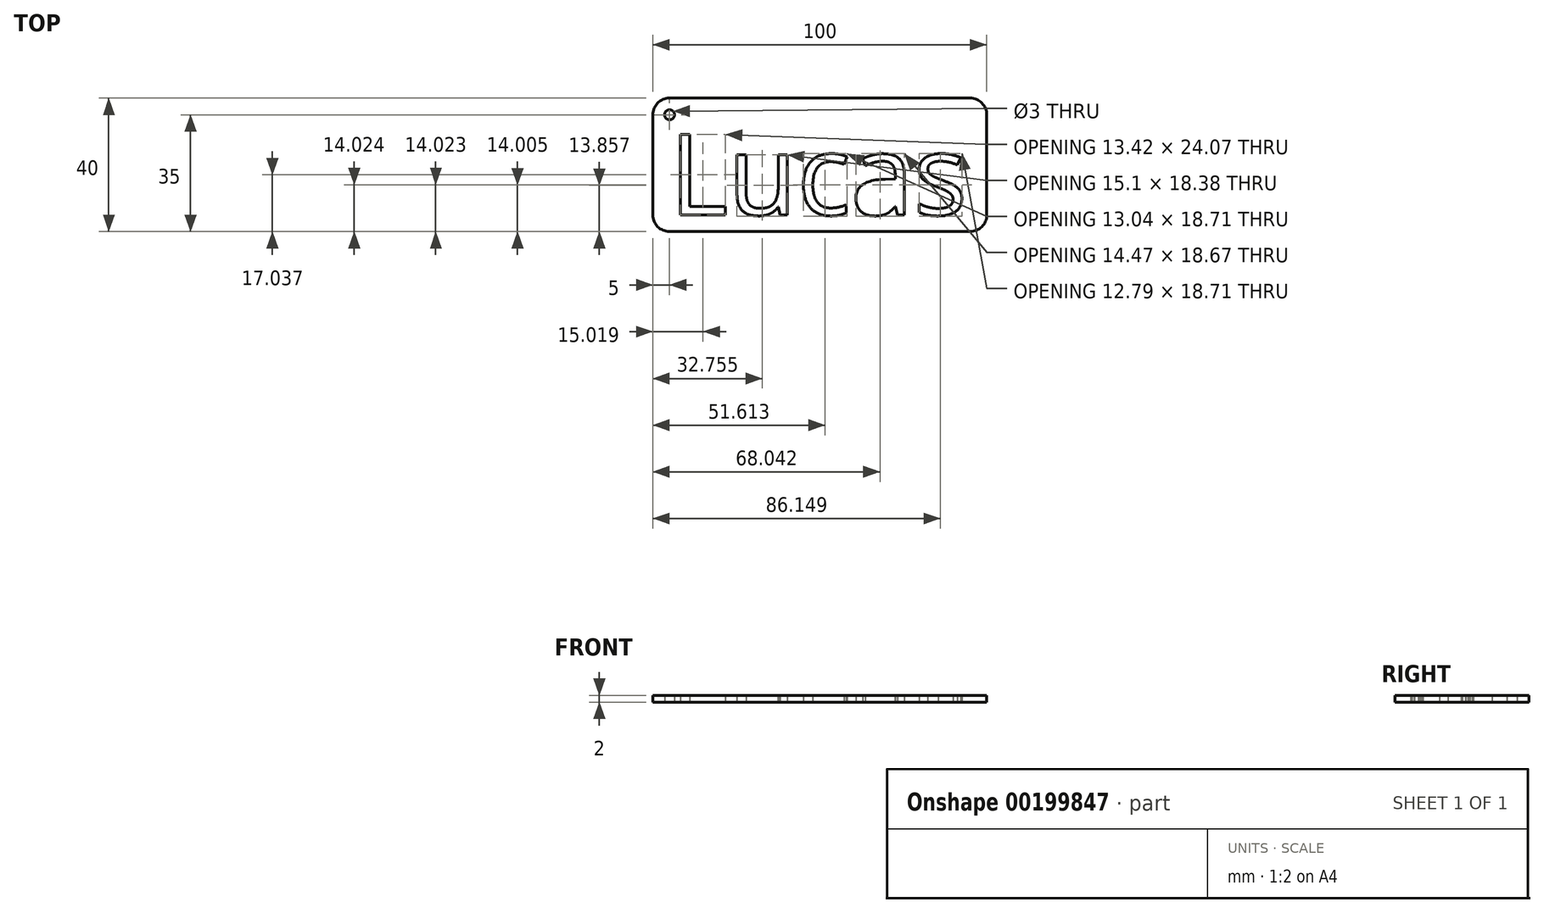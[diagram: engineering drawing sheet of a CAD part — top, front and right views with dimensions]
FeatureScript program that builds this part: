
annotation { "Feature Type Name" : "Feature", "Feature Type Description" : "" }
export const myFeature = defineFeature(function(context is Context, id is Id, definition is map)
    precondition{}
    {
        {
            var Q0;
            Q0=qCreatedBy(makeId("Top.planeOp"),FACE);
            var sketch = newSketch(context, id + "F0", { "sketchPlane" : qUnion([Q0])});
            skLineSegment(sketch, "E0.bottom", {"start": v(5, 0) * mm, "end": v(95, 0) * mm});
            skLineSegment(sketch, "E0.top", {"start": v(5, 40) * mm, "end": v(95, 40) * mm});
            skLineSegment(sketch, "E0.left", {"start": v(0, 5) * mm, "end": v(0, 35) * mm});
            skLineSegment(sketch, "E0.right", {"start": v(100, 5) * mm, "end": v(100, 35) * mm});
            skPoint(sketch, "E1.visualSharp", {"position": v(0, 0) * mm});
            skArc(sketch, "E1.filletArc", {"start": v(0, 5) * mm, "mid": v(1.46, 1.46) * mm, "end": v(5, 0) * mm});
            skPoint(sketch, "E2.visualSharp", {"position": v(100, 0) * mm});
            skArc(sketch, "E2.filletArc", {"start": v(95, 0) * mm, "mid": v(98.54, 1.46) * mm, "end": v(100, 5) * mm});
            skPoint(sketch, "E3.visualSharp", {"position": v(100, 40) * mm});
            skArc(sketch, "E3.filletArc", {"start": v(100, 35) * mm, "mid": v(98.54, 38.54) * mm, "end": v(95, 40) * mm});
            skPoint(sketch, "E4.visualSharp", {"position": v(0, 40) * mm});
            skArc(sketch, "E4.filletArc", {"start": v(5, 40) * mm, "mid": v(1.46, 38.54) * mm, "end": v(0, 35) * mm});
            skCircle(sketch, "E5", {"center": v(5, 35) * mm, "radius": 1.5 * mm});
            skText(sketch, "E6", { "text": "Lucas", "fontName": "OpenSans-Regular.ttf"});
            const initialGuessF0  = {"E6": [0.005, 0.005, 1, 0, 0.02428]};
            skSetInitialGuess(sketch, initialGuessF0);
            skSolve(sketch);
        }
        {
            var Q0;
            Q0 = qSketchRegion(id + "F0", true);
            extrude(context, id + "F1", {"entities" : qUnion([Q0]), "depth" : 2 * mm});
        }
    });
